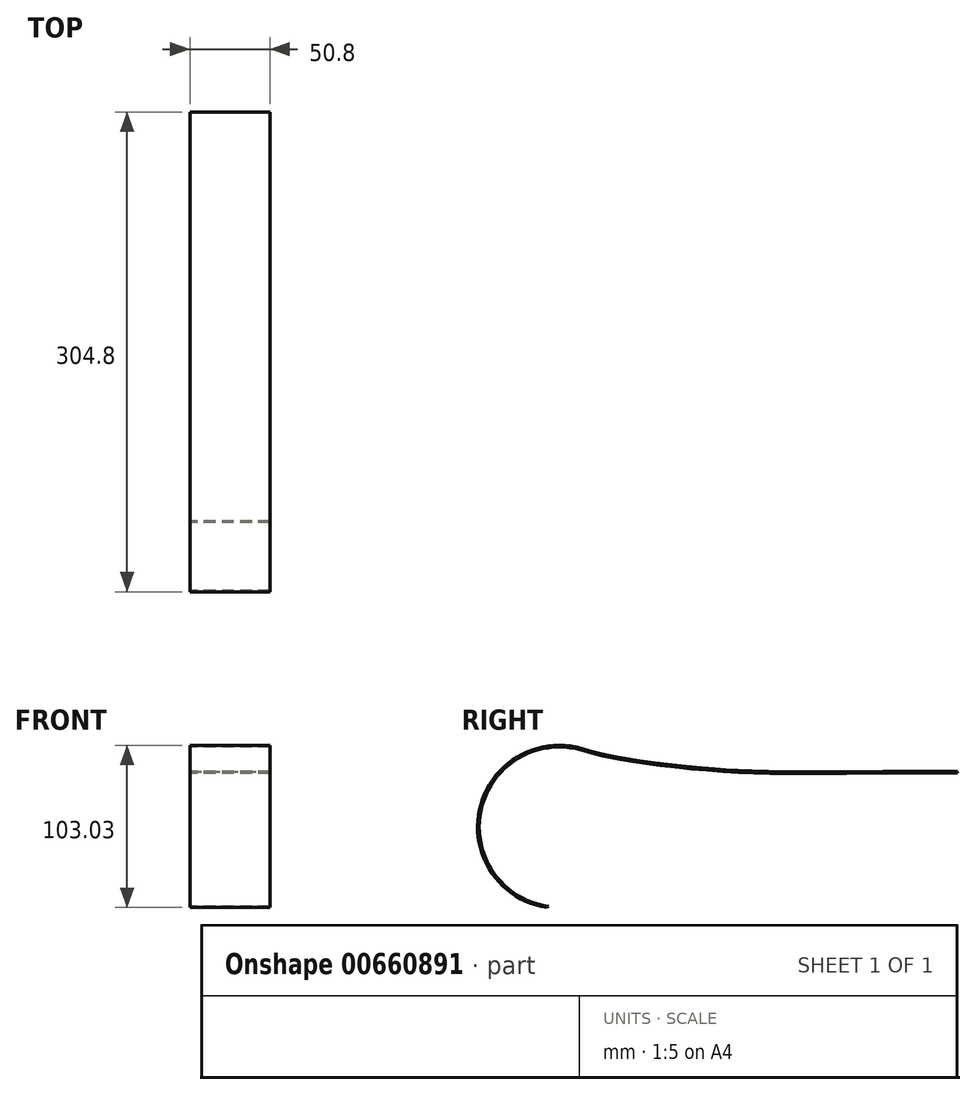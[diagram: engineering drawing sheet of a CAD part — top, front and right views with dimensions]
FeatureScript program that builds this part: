
annotation { "Feature Type Name" : "Feature", "Feature Type Description" : "" }
export const myFeature = defineFeature(function(context is Context, id is Id, definition is map)
    precondition{}
    {
        {
            var Q0;
            Q0=qCreatedBy(makeId("Right.planeOp"),FACE);
            var sketch = newSketch(context, id + "F0", { "sketchPlane" : qUnion([Q0])});
            skLineSegment(sketch, "E0", {"start": v(0, 0) * mm, "end": v(0, -50.8) * mm});
            skArc(sketch, "E1", {"start": v(20.68, 99.22) * mm, "mid": v(-42.87, 60.7) * mm, "end": v(0, 0) * mm});
            skFitSpline(sketch, "E2", {"points": [v(20.68, 99.22) * mm, v(40.2, 94.31) * mm, v(107.5, 85.9) * mm, v(259.85, 84.7) * mm], "startDerivative": vector(112.78, -31.93) * mm, "endDerivative": vector(496.64, 0) * mm});
            skLineSegment(sketch, "E3", {"start": v(-44.95, 94.31) * mm, "end": v(-44.95, 12.72) * mm, "construction": true});
            skLineSegment(sketch, "E4.0", {"start": v(-1.02, -0.88) * mm, "end": v(-1.02, -50.8) * mm});
            skArc(sketch, "E4.1", {"start": v(20.96, 100.2) * mm, "mid": v(-43.77, 61.34) * mm, "end": v(-1.02, -0.88) * mm});
            skFitSpline(sketch, "E4.2", {"points": [v(20.96, 100.2) * mm, v(23.3, 99.53) * mm, v(26.44, 98.63) * mm, v(30.55, 97.52) * mm, v(33.78, 96.72) * mm, v(36.76, 96.05) * mm, v(39.4, 95.5) * mm, v(41.55, 95.08) * mm, v(43.86, 94.65) * mm, v(47.13, 94.07) * mm, v(51.58, 93.33) * mm, v(57.4, 92.43) * mm, v(65.74, 91.24) * mm, v(77.02, 89.8) * mm, v(88.96, 88.5) * mm, v(98.63, 87.61) * mm, v(104.65, 87.12) * mm, v(109.42, 86.78) * mm, v(114.16, 86.47) * mm, v(120.06, 86.15) * mm, v(127.17, 85.84) * mm, v(136.8, 85.54) * mm, v(149.34, 85.33) * mm, v(165.82, 85.28) * mm, v(184.38, 85.37) * mm, v(212.78, 85.57) * mm, v(239.15, 85.72) * mm, v(259.85, 85.72) * mm]});
            skLineSegment(sketch, "E5", {"start": v(0, -50.8) * mm, "end": v(-1.02, -50.8) * mm});
            skLineSegment(sketch, "E6", {"start": v(259.85, 85.72) * mm, "end": v(259.85, 84.7) * mm});
            skPoint(sketch, "E7", {"position": v(-44.95, 50.33) * mm});
            skLineSegment(sketch, "E8", {"start": v(-1.02, -0.88) * mm, "end": v(0, 0) * mm});
            skSolve(sketch);
        }
        {
            var Q0;
            Q0=makeQuery(id+"F0.imprint","IMPRINT",FACE,{"disambiguationData":[TD([[makeQuery(id+"F0.imprint","IMPRINT",EDGE,{"derivedFrom":sQuery(id+"F0.wireOp",EDGE,"E1")}),-1.0]])]});
            extrude(context, id + "F1", {"entities" : qUnion([Q0]), "depth" : 25.4 * mm, "offsetDistance" : 25.4 * mm, "hasSecondDirection" : true, "secondDirectionOppositeDirection" : true, "secondDirectionDepth" : 25.4 * mm});
        }
    });
